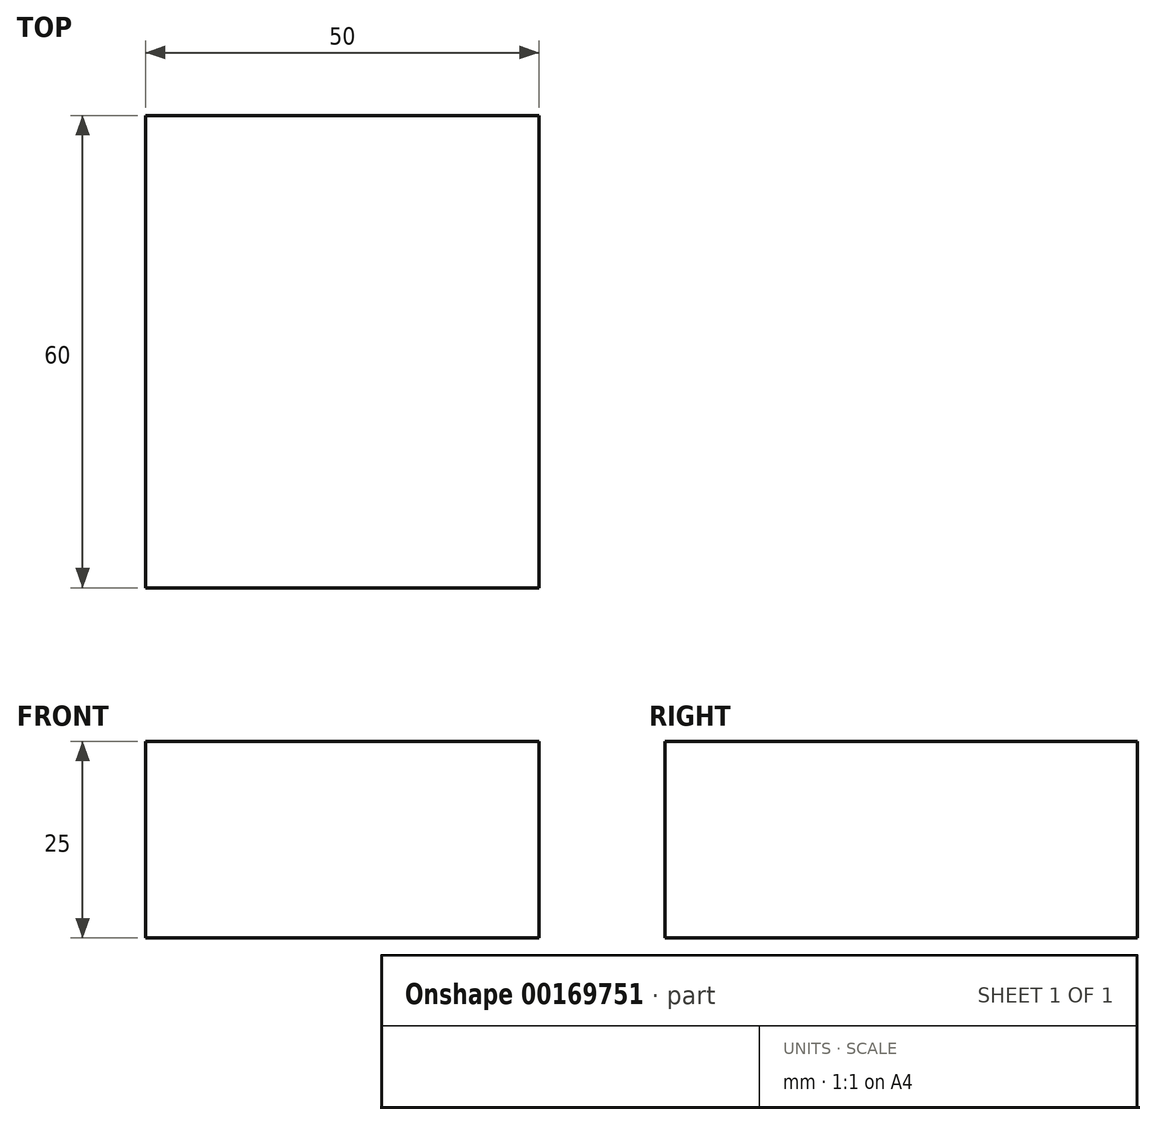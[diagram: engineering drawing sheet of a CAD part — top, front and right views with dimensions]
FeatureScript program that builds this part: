
annotation { "Feature Type Name" : "Feature", "Feature Type Description" : "" }
export const myFeature = defineFeature(function(context is Context, id is Id, definition is map)
    precondition{}
    {
        {
            var Q0;
            Q0=qCreatedBy(makeId("Top.planeOp"),FACE);
            var sketch = newSketch(context, id + "F0", { "sketchPlane" : qUnion([Q0])});
            skLineSegment(sketch, "E0.bottom", {"start": v(-24.6, 36.85) * mm, "end": v(25.4, 36.85) * mm});
            skLineSegment(sketch, "E0.top", {"start": v(-24.6, -23.15) * mm, "end": v(25.4, -23.15) * mm});
            skLineSegment(sketch, "E0.left", {"start": v(-24.6, 36.85) * mm, "end": v(-24.6, -23.15) * mm});
            skLineSegment(sketch, "E0.right", {"start": v(25.4, 36.85) * mm, "end": v(25.4, -23.15) * mm});
            skSolve(sketch);
        }
        {
            var Q0;
            Q0=makeQuery(id+"F0.imprint","IMPRINT",FACE,{"disambiguationData":[TD([[makeQuery(id+"F0.imprint","IMPRINT",EDGE,{"derivedFrom":sQuery(id+"F0.wireOp",EDGE,"E0.bottom")}),-1.0]])]});
            extrude(context, id + "F1", {"entities" : qUnion([Q0]), "depth" : 25 * mm});
        }
    });
